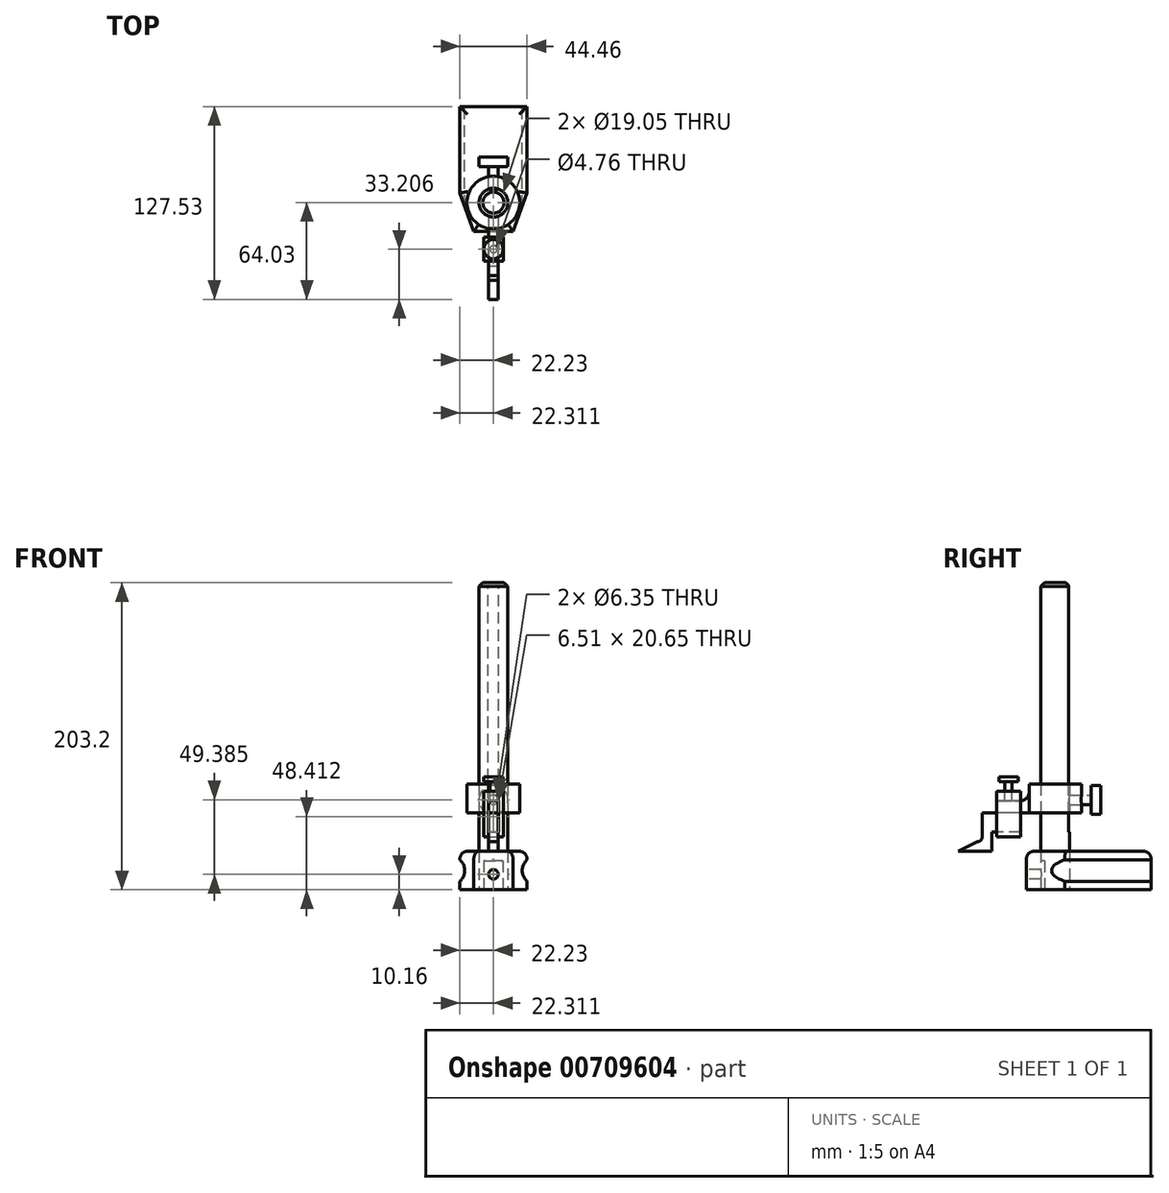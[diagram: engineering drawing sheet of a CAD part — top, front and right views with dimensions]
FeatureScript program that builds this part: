
annotation { "Feature Type Name" : "Feature", "Feature Type Description" : "" }
export const myFeature = defineFeature(function(context is Context, id is Id, definition is map)
    precondition{}
    {
        {
            var Q0;
            Q0=qCreatedBy(makeId("Top.planeOp"),FACE);
            var sketch = newSketch(context, id + "F0", { "sketchPlane" : qUnion([Q0])});
            skCircle(sketch, "E0", {"center": v(0, 0) * mm, "radius": 9.52 * mm});
            skLineSegment(sketch, "E1", {"start": v(0, 63.5) * mm, "end": v(-22.23, 63.5) * mm});
            skLineSegment(sketch, "E2", {"start": v(-22.23, 63.5) * mm, "end": v(-22.22, 6.35) * mm});
            skLineSegment(sketch, "E3", {"start": v(-22.23, 6.35) * mm, "end": v(-12.98, -19.05) * mm});
            skLineSegment(sketch, "E4", {"start": v(-12.98, -19.05) * mm, "end": v(0, -19.05) * mm});
            skLineSegment(sketch, "E5.MirrorCS", {"start": v(0, 63.5) * mm, "end": v(22.23, 63.5) * mm});
            skLineSegment(sketch, "E6.MirrorCS", {"start": v(22.23, 63.5) * mm, "end": v(22.23, 6.35) * mm});
            skLineSegment(sketch, "E7.MirrorCS", {"start": v(22.22, 6.35) * mm, "end": v(12.98, -19.05) * mm});
            skLineSegment(sketch, "E8.MirrorCS", {"start": v(12.98, -19.05) * mm, "end": v(0, -19.05) * mm});
            skSolve(sketch);
        }
        {
            var Q0;
            Q0 = qSketchRegion(id + "F0", true);
            extrude(context, id + "F1", {"entities" : qUnion([Q0]), "depth" : 25.4 * mm, "offsetDistance" : 25.4 * mm});
        }
        {
            var Q0;
            Q0=makeQuery(id+"F1.opExtrude","SWEPT_FACE",FACE,{"disambiguationData":[OSD([sQuery(id+"F0.wireOp",EDGE,"E1"),sQuery(id+"F0.wireOp",EDGE,"E5.MirrorCS")])]});
            var sketch = newSketch(context, id + "F2", { "sketchPlane" : qUnion([Q0])});
            skCircle(sketch, "E9", {"center": v(-28.58, 12.7) * mm, "radius": 9.53 * mm});
            skPoint(sketch, "E9.centerSnap0", {"position": v(-22.23, 12.7) * mm});
            skCircle(sketch, "E10.MirrorC", {"center": v(28.57, 12.7) * mm, "radius": 9.53 * mm});
            skSolve(sketch);
        }
        {
            var Q0;
            Q0 = qSketchRegion(id + "F2", true);
            extrude(context, id + "F3", {"entities" : qUnion([Q0]), "operationType" : NewBodyOperationType.REMOVE, "oppositeDirection" : true, "depth" : 76.2 * mm, "offsetDistance" : 25.4 * mm});
        }
        {
            var Q0;
            Q0=qCreatedBy(makeId("Top.planeOp"),FACE);
            var sketch = newSketch(context, id + "F4", { "sketchPlane" : qUnion([Q0])});
            skCircle(sketch, "E11", {"center": v(0, 0) * mm, "radius": 9.53 * mm});
            skSolve(sketch);
        }
        {
            var Q0;
            Q0 = qSketchRegion(id + "F4", true);
            extrude(context, id + "F5", {"entities" : qUnion([Q0]), "depth" : 203.2 * mm, "offsetDistance" : 25.4 * mm});
        }
        {
            var Q0;
            Q0=qCreatedBy(makeId("Top.planeOp"),FACE);
            cPlane(context, id + "F6", {"entities" : qUnion([Q0]), "cplaneType" : CPlaneType.OFFSET, "offset" : 50.8 * mm, "width" : 152.4 * mm, "height" : 152.4 * mm});
        }
        {
            var Q0;
            Q0=qCreatedBy(id+"F6.planeOp",FACE);
            var sketch = newSketch(context, id + "F7", { "sketchPlane" : qUnion([Q0])});
            skCircle(sketch, "E12", {"center": v(0, 0) * mm, "radius": 9.52 * mm});
            skArc(sketch, "E13", {"start": v(3.17, -17.17) * mm, "mid": v(0, 17.46) * mm, "end": v(-3.18, -17.17) * mm});
            skLineSegment(sketch, "E14", {"start": v(-3.18, -17.17) * mm, "end": v(-3.17, -38.76) * mm});
            skLineSegment(sketch, "E15", {"start": v(-3.17, -38.76) * mm, "end": v(0, -38.76) * mm});
            skLineSegment(sketch, "E16.MirrorCS", {"start": v(3.18, -17.17) * mm, "end": v(3.17, -38.76) * mm});
            skLineSegment(sketch, "E17.MirrorCS", {"start": v(3.17, -38.76) * mm, "end": v(0, -38.76) * mm});
            skSolve(sketch);
        }
        {
            var Q0;
            Q0 = qSketchRegion(id + "F7", true);
            extrude(context, id + "F8", {"entities" : qUnion([Q0]), "depth" : 19.05 * mm, "offsetDistance" : 25.4 * mm});
        }
        {
            var Q0;
            Q0=makeQuery(id+"F8.opExtrude","SWEPT_FACE",FACE,{"disambiguationData":[OSD([sQuery(id+"F7.wireOp",EDGE,"E16.MirrorCS")])]});
            var sketch = newSketch(context, id + "F9", { "sketchPlane" : qUnion([Q0])});
            skLineSegment(sketch, "E18", {"start": v(-38.76, 58.74) * mm, "end": v(-23.52, 58.74) * mm});
            skLineSegment(sketch, "E19", {"start": v(-17.17, 65.09) * mm, "end": v(-17.17, 69.85) * mm});
            skLineSegment(sketch, "E20", {"start": v(-17.17, 69.85) * mm, "end": v(-38.76, 69.85) * mm});
            skLineSegment(sketch, "E21", {"start": v(-38.76, 69.85) * mm, "end": v(-38.76, 58.74) * mm});
            skPoint(sketch, "E22.visualSharp", {"position": v(-17.17, 58.74) * mm});
            skArc(sketch, "E22.filletArc", {"start": v(-23.52, 58.74) * mm, "mid": v(-19.03, 60.6) * mm, "end": v(-17.17, 65.09) * mm});
            skSolve(sketch);
        }
        {
            var Q0;
            Q0 = qSketchRegion(id + "F9", true);
            extrude(context, id + "F10", {"entities" : qUnion([Q0]), "operationType" : NewBodyOperationType.REMOVE, "oppositeDirection" : true, "depth" : 25.4 * mm, "offsetDistance" : 25.4 * mm});
        }
        {
            var Q0;
            Q0=makeQuery(id+"F8.opExtrude","SWEPT_FACE",FACE,{"disambiguationData":[OSD([sQuery(id+"F7.wireOp",EDGE,"E16.MirrorCS")])]});
            var sketch = newSketch(context, id + "F11", { "sketchPlane" : qUnion([Q0])});
            skLineSegment(sketch, "E23", {"start": v(-26.06, 50.8) * mm, "end": v(-48.29, 50.8) * mm});
            skLineSegment(sketch, "E24", {"start": v(-48.29, 50.8) * mm, "end": v(-48.29, 34.93) * mm});
            skLineSegment(sketch, "E25", {"start": v(-51.46, 31.75) * mm, "end": v(-51.46, 31.75) * mm});
            skLineSegment(sketch, "E26", {"start": v(-22.89, 50.8) * mm, "end": v(-22.89, 38.1) * mm});
            skLineSegment(sketch, "E27", {"start": v(-22.89, 38.1) * mm, "end": v(-41.94, 38.1) * mm});
            skLineSegment(sketch, "E28", {"start": v(-41.94, 38.1) * mm, "end": v(-41.94, 25.4) * mm});
            skLineSegment(sketch, "E29", {"start": v(-41.94, 25.4) * mm, "end": v(-64.03, 25.4) * mm});
            skLineSegment(sketch, "E30", {"start": v(-64.03, 25.4) * mm, "end": v(-51.46, 31.75) * mm});
            skPoint(sketch, "E31.visualSharp", {"position": v(-48.29, 31.75) * mm});
            skArc(sketch, "E31.filletArc", {"start": v(-51.46, 31.75) * mm, "mid": v(-49.22, 32.68) * mm, "end": v(-48.29, 34.93) * mm});
            skSolve(sketch);
        }
        {
            var Q0;
            Q0 = qSketchRegion(id + "F11", true);
            var Q1;
            {var subQ5=sQuery(id+"F11.wireOp",EDGE,"E24");Q1=makeQuery(id+"F11.imprint","IMPRINT",FACE,{"disambiguationData":[TD([[makeQuery(id+"F11.imprint","IMPRINT",EDGE,{"derivedFrom":subQ5}),1.0]])]});}
            extrude(context, id + "F12", {"entities" : qUnion([Q0, Q1]), "oppositeDirection" : true, "depth" : 6.35 * mm, "offsetDistance" : 25.4 * mm});
        }
        {
            var Q0;
            Q0=makeQuery(id+"F1.opExtrude","CAP_EDGE",EDGE,{"disambiguationData":[OSD([sQuery(id+"F0.wireOp",EDGE,"E2")])],"isStart":false});
            var Q1;
            Q1=makeQuery(id+"F1.opExtrude","CAP_EDGE",EDGE,{"disambiguationData":[OSD([sQuery(id+"F0.wireOp",EDGE,"E1"),sQuery(id+"F0.wireOp",EDGE,"E5.MirrorCS")])],"isStart":false});
            var Q2;
            Q2=makeQuery(id+"F1.opExtrude","CAP_EDGE",EDGE,{"disambiguationData":[OSD([sQuery(id+"F0.wireOp",EDGE,"E6.MirrorCS")])],"isStart":false});
            var Q3;
            Q3=makeQuery(id+"F1.opExtrude","CAP_EDGE",EDGE,{"disambiguationData":[OSD([sQuery(id+"F0.wireOp",EDGE,"E7.MirrorCS")])],"isStart":false});
            var Q4;
            Q4=makeQuery(id+"F1.opExtrude","CAP_EDGE",EDGE,{"disambiguationData":[OSD([sQuery(id+"F0.wireOp",EDGE,"E4"),sQuery(id+"F0.wireOp",EDGE,"E8.MirrorCS")])],"isStart":false});
            var Q5;
            Q5=makeQuery(id+"F1.opExtrude","CAP_EDGE",EDGE,{"disambiguationData":[OSD([sQuery(id+"F0.wireOp",EDGE,"E3")])],"isStart":false});
            fillet(context, id + "F13", {"entities" : qUnion([Q0, Q1, Q2, Q3, Q4, Q5]), "radius" : 5.08 * mm, "tangentPropagation" : true, "allowEdgeOverflow" : false});
        }
        {
            var Q0;
            Q0=makeQuery(id+"F8.opExtrude","SWEPT_FACE",FACE,{"disambiguationData":[OSD([sQuery(id+"F7.wireOp",EDGE,"E15"),sQuery(id+"F7.wireOp",EDGE,"E17.MirrorCS")])]});
            var sketch = newSketch(context, id + "F14", { "sketchPlane" : qUnion([Q0])});
            skLineSegment(sketch, "E32.bottom", {"start": v(-3.18, 58.74) * mm, "end": v(3.34, 58.74) * mm});
            skLineSegment(sketch, "E32.top", {"start": v(-3.18, 38.09) * mm, "end": v(3.34, 38.09) * mm});
            skLineSegment(sketch, "E32.left", {"start": v(-3.18, 58.74) * mm, "end": v(-3.18, 38.09) * mm});
            skLineSegment(sketch, "E32.right", {"start": v(3.34, 58.74) * mm, "end": v(3.34, 38.09) * mm});
            skLineSegment(sketch, "E33.0", {"start": v(-6.35, 65.09) * mm, "end": v(-6.35, 34.91) * mm});
            skLineSegment(sketch, "E34.0", {"start": v(6.51, 65.09) * mm, "end": v(6.51, 34.91) * mm});
            skLineSegment(sketch, "E35.0", {"start": v(-6.35, 34.91) * mm, "end": v(3.17, 34.91) * mm});
            skLineSegment(sketch, "E36.0", {"start": v(-6.35, 65.09) * mm, "end": v(6.51, 65.09) * mm});
            skLineSegment(sketch, "E37", {"start": v(6.51, 34.91) * mm, "end": v(3.17, 34.91) * mm});
            skSolve(sketch);
        }
        {
            var Q0;
            Q0 = qSketchRegion(id + "F14", true);
            extrude(context, id + "F15", {"entities" : qUnion([Q0]), "oppositeDirection" : true, "depth" : 15.88 * mm, "offsetDistance" : 25.4 * mm});
        }
        {
            var Q0;
            Q0=makeQuery(id+"F5.opExtrude","CAP_FACE",FACE,{"disambiguationData":[OSD([sQuery(id+"F4.wireOp",EDGE,"E11")])],"isStart":false});
            var sketch = newSketch(context, id + "F16", { "sketchPlane" : qUnion([Q0])});
            skLineSegment(sketch, "E38", {"start": v(-3.42, 8.9) * mm, "end": v(3.42, 8.9) * mm});
            skArc(sketch, "E39", {"start": v(3.42, 8.9) * mm, "mid": v(0, 9.53) * mm, "end": v(-3.42, 8.9) * mm});
            skSolve(sketch);
        }
        {
            var Q0;
            Q0=makeQuery(id+"F16.imprint","IMPRINT",FACE,{"disambiguationData":[TD([[makeQuery(id+"F16.imprint","IMPRINT",EDGE,{"derivedFrom":sQuery(id+"F16.wireOp",EDGE,"E38")}),1.0]])]});
            extrude(context, id + "F17", {"entities" : qUnion([Q0]), "operationType" : NewBodyOperationType.REMOVE, "oppositeDirection" : true, "depth" : 165.1 * mm, "offsetDistance" : 25.4 * mm});
        }
        {
            var Q0;
            Q0=qCreatedBy(makeId("Front.planeOp"),FACE);
            cPlane(context, id + "F18", {"entities" : qUnion([Q0]), "cplaneType" : CPlaneType.OFFSET, "offset" : 17.46 * mm, "oppositeDirection" : true, "width" : 152.4 * mm, "height" : 152.4 * mm});
        }
        {
            var Q0;
            Q0=qCreatedBy(id+"F18.planeOp",FACE);
            var sketch = newSketch(context, id + "F19", { "sketchPlane" : qUnion([Q0])});
            skCircle(sketch, "E40", {"center": v(0, 59.54) * mm, "radius": 3.18 * mm});
            skSolve(sketch);
        }
        {
            var Q0;
            Q0 = qSketchRegion(id + "F19", true);
            extrude(context, id + "F20", {"entities" : qUnion([Q0]), "operationType" : NewBodyOperationType.REMOVE, "endBound" : BoundingType.UP_TO_NEXT, "depth" : 25.4 * mm, "offsetDistance" : 25.4 * mm});
        }
        {
            var Q0;
            Q0=makeQuery(id+"F15.opExtrude","SWEPT_FACE",FACE,{"disambiguationData":[OSD([sQuery(id+"F14.wireOp",EDGE,"E36.0")])]});
            var sketch = newSketch(context, id + "F21", { "sketchPlane" : qUnion([Q0])});
            skCircle(sketch, "E41", {"center": v(0.08, -30.82) * mm, "radius": 2.38 * mm});
            skPoint(sketch, "E41.centerSnap0", {"position": v(0.08, -38.76) * mm});
            skPoint(sketch, "E41.centerSnap1", {"position": v(-6.35, -30.82) * mm});
            skSolve(sketch);
        }
        {
            var Q0;
            Q0 = qSketchRegion(id + "F21", true);
            extrude(context, id + "F22", {"entities" : qUnion([Q0]), "operationType" : NewBodyOperationType.REMOVE, "endBound" : BoundingType.UP_TO_NEXT, "oppositeDirection" : true, "depth" : 25.4 * mm, "offsetDistance" : 25.4 * mm});
        }
        {
            var Q0;
            Q0=makeQuery(id+"F5.opExtrude","CAP_EDGE",EDGE,{"disambiguationData":[OSD([sQuery(id+"F4.wireOp",EDGE,"E11")])],"isStart":false});
            chamfer(context, id + "F23", {"entities" : qUnion([Q0]), "width" : 2.54 * mm, "tangentPropagation" : true});
        }
        {
            var Q0;
            Q0=makeQuery(id+"F1.opExtrude","SWEPT_FACE",FACE,{"disambiguationData":[OSD([sQuery(id+"F0.wireOp",EDGE,"E4"),sQuery(id+"F0.wireOp",EDGE,"E8.MirrorCS")])]});
            var sketch = newSketch(context, id + "F24", { "sketchPlane" : qUnion([Q0])});
            skCircle(sketch, "E42", {"center": v(0, 10.16) * mm, "radius": 3.18 * mm});
            skPoint(sketch, "E42.centerSnap0", {"position": v(0, 20.32) * mm});
            skPoint(sketch, "E42.centerSnap1", {"position": v(12.98, 10.16) * mm});
            skSolve(sketch);
        }
        {
            var Q0;
            Q0 = qSketchRegion(id + "F24", true);
            extrude(context, id + "F25", {"entities" : qUnion([Q0]), "operationType" : NewBodyOperationType.REMOVE, "endBound" : BoundingType.UP_TO_NEXT, "oppositeDirection" : true, "depth" : 25.4 * mm, "offsetDistance" : 25.4 * mm});
        }
        {
            var Q0;
            Q0=makeQuery(id+"F0.imprint","IMPRINT",FACE,{"disambiguationData":[TD([[makeQuery(id+"F0.imprint","IMPRINT",EDGE,{"derivedFrom":sQuery(id+"F0.wireOp",EDGE,"E0")}),1.0]])]});
            var sketch = newSketch(context, id + "F26", { "sketchPlane" : qUnion([Q0])});
            skArc(sketch, "E43.0", {"start": v(-6.32, -7.12) * mm, "mid": v(0, -9.52) * mm, "end": v(6.32, -7.12) * mm});
            skLineSegment(sketch, "E44", {"start": v(6.32, -7.12) * mm, "end": v(-6.32, -7.12) * mm});
            skSolve(sketch);
        }
        {
            var Q0;
            Q0 = qSketchRegion(id + "F26", true);
            extrude(context, id + "F27", {"entities" : qUnion([Q0]), "operationType" : NewBodyOperationType.REMOVE, "depth" : 19.05 * mm, "offsetDistance" : 25.4 * mm});
        }
        {
            var Q0;
            Q0=qCreatedBy(id+"F18.planeOp",FACE);
            var sketch = newSketch(context, id + "F28", { "sketchPlane" : qUnion([Q0])});
            skCircle(sketch, "E45.0", {"center": v(0, 59.54) * mm, "radius": 3.18 * mm});
            skSolve(sketch);
        }
        {
            var Q0;
            Q0 = qSketchRegion(id + "F28", true);
            extrude(context, id + "F29", {"entities" : qUnion([Q0]), "depth" : 7.94 * mm, "offsetDistance" : 25.4 * mm, "hasSecondDirection" : true, "secondDirectionOppositeDirection" : true, "secondDirectionDepth" : 6.35 * mm});
        }
        {
            var Q0;
            Q0=makeQuery(id+"F29.opExtrude","CAP_FACE",FACE,{"disambiguationData":[OSD([sQuery(id+"F28.wireOp",EDGE,"E45.0")])],"isStart":true});
            var sketch = newSketch(context, id + "F30", { "sketchPlane" : qUnion([Q0])});
            skCircle(sketch, "E46", {"center": v(0, 59.54) * mm, "radius": 9.53 * mm});
            skSolve(sketch);
        }
        {
            var Q0;
            Q0 = qSketchRegion(id + "F30", true);
            extrude(context, id + "F31", {"entities" : qUnion([Q0]), "operationType" : NewBodyOperationType.ADD, "depth" : 6.35 * mm, "offsetDistance" : 25.4 * mm});
        }
        {
            var Q0;
            Q0=makeQuery(id+"F15.opExtrude","SWEPT_FACE",FACE,{"disambiguationData":[OSD([sQuery(id+"F14.wireOp",EDGE,"E36.0")])]});
            var sketch = newSketch(context, id + "F32", { "sketchPlane" : qUnion([Q0])});
            skCircle(sketch, "E47", {"center": v(0.08, -30.82) * mm, "radius": 2.38 * mm});
            skSolve(sketch);
        }
        {
            var Q0;
            Q0 = qSketchRegion(id + "F32", true);
            extrude(context, id + "F33", {"entities" : qUnion([Q0]), "oppositeDirection" : true, "depth" : 6.35 * mm, "offsetDistance" : 25.4 * mm, "hasSecondDirection" : true, "secondDirectionOppositeDirection" : false, "secondDirectionDepth" : 6.35 * mm});
        }
        {
            var Q0;
            Q0=makeQuery(id+"F33.opExtrude","CAP_FACE",FACE,{"disambiguationData":[OSD([sQuery(id+"F32.wireOp",EDGE,"E47")])],"isStart":true});
            var sketch = newSketch(context, id + "F34", { "sketchPlane" : qUnion([Q0])});
            skCircle(sketch, "E48", {"center": v(0.08, -30.82) * mm, "radius": 6.35 * mm});
            skSolve(sketch);
        }
        {
            var Q0;
            Q0 = qSketchRegion(id + "F34", true);
            extrude(context, id + "F35", {"entities" : qUnion([Q0]), "operationType" : NewBodyOperationType.ADD, "depth" : 3.17 * mm, "offsetDistance" : 25.4 * mm});
        }
    });
